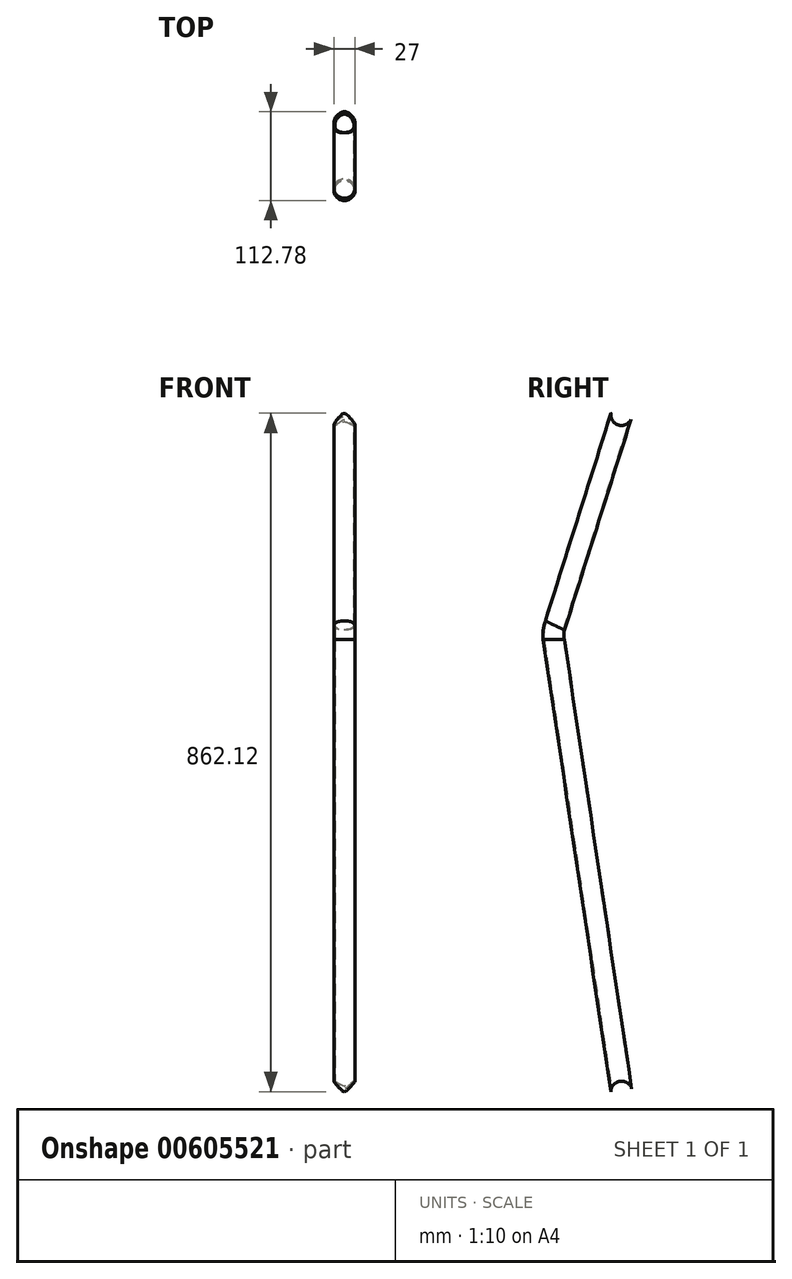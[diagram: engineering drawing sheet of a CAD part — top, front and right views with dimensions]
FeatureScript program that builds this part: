
annotation { "Feature Type Name" : "Feature", "Feature Type Description" : "" }
export const myFeature = defineFeature(function(context is Context, id is Id, definition is map)
    precondition{}
    {
        {
            var Q0;
            Q0=qCreatedBy(makeId("Top.planeOp"),FACE);
            var sketch = newSketch(context, id + "F0", { "sketchPlane" : qUnion([Q0])});
            skCircle(sketch, "E0", {"center": v(0, 0) * mm, "radius": 12.25 * mm});
            skCircle(sketch, "E1", {"center": v(0, 0) * mm, "radius": 13.5 * mm});
            skSolve(sketch);
        }
        {
            var Q0;
            Q0=qCreatedBy(makeId("Right.planeOp"),FACE);
            var sketch = newSketch(context, id + "F1", { "sketchPlane" : qUnion([Q0])});
            skLineSegment(sketch, "E2", {"start": v(0, 0) * mm, "end": v(0, 860) * mm});
            skLineSegment(sketch, "E3", {"start": v(0, 0) * mm, "end": v(-86.04, 574.33) * mm});
            skLineSegment(sketch, "E4", {"start": v(-84.62, 592.32) * mm, "end": v(0, 860) * mm});
            skPoint(sketch, "E5.visualSharp", {"position": v(-87.41, 583.49) * mm});
            skArc(sketch, "E5.filletArc", {"start": v(-84.62, 592.32) * mm, "mid": v(-86.36, 583.4) * mm, "end": v(-86.04, 574.33) * mm});
            skSolve(sketch);
        }
        {
            var Q0;
            Q0=makeQuery(id+"F0.imprint","IMPRINT",FACE,{"disambiguationData":[TD([[makeQuery(id+"F0.imprint","IMPRINT",EDGE,{"derivedFrom":sQuery(id+"F0.wireOp",EDGE,"E0")}),-1.0]])]});
            var Q1;
            Q1=sQuery(id+"F1.wireOp",EDGE,"E3");
            var Q2;
            Q2=sQuery(id+"F1.wireOp",EDGE,"E5.filletArc");
            var Q3;
            Q3=sQuery(id+"F1.wireOp",EDGE,"E4");
            sweep(context, id + "F2", {"profiles" : qUnion([Q0]), "path" : qUnion([Q1, Q2, Q3])});
        }
        {
            var Q0;
            Q0=qCreatedBy(makeId("Right.planeOp"),FACE);
            var sketch = newSketch(context, id + "F3", { "sketchPlane" : qUnion([Q0])});
            skCircle(sketch, "E6", {"center": v(0, 0) * mm, "radius": 13.5 * mm});
            skSolve(sketch);
        }
        {
            var Q0;
            Q0=makeQuery(id+"F3.imprint","IMPRINT",FACE,{"disambiguationData":[TD([[makeQuery(id+"F3.imprint","IMPRINT",EDGE,{"derivedFrom":sQuery(id+"F3.wireOp",EDGE,"E6")}),1.0]])]});
            extrude(context, id + "F4", {"entities" : qUnion([Q0]), "operationType" : NewBodyOperationType.REMOVE, "depth" : 25 * mm, "offsetDistance" : 25 * mm, "hasSecondDirection" : true, "secondDirectionOppositeDirection" : true, "secondDirectionDepth" : 25 * mm});
        }
        {
            var Q0;
            Q0=qCreatedBy(makeId("Right.planeOp"),FACE);
            var sketch = newSketch(context, id + "F5", { "sketchPlane" : qUnion([Q0])});
            skLineSegment(sketch, "E7", {"start": v(0, 0) * mm, "end": v(0, 860) * mm});
            skCircle(sketch, "E8", {"center": v(0, 860) * mm, "radius": 13.5 * mm});
            skSolve(sketch);
        }
        {
            var Q0;
            Q0=makeQuery(id+"F5.imprint","IMPRINT",FACE,{"disambiguationData":[TD([[makeQuery(id+"F5.imprint","IMPRINT",EDGE,{"derivedFrom":sQuery(id+"F5.wireOp",EDGE,"E8")}),1.0]])]});
            extrude(context, id + "F6", {"entities" : qUnion([Q0]), "operationType" : NewBodyOperationType.REMOVE, "depth" : 25 * mm, "offsetDistance" : 25 * mm, "hasSecondDirection" : true, "secondDirectionOppositeDirection" : true, "secondDirectionDepth" : 25 * mm});
        }
    });
